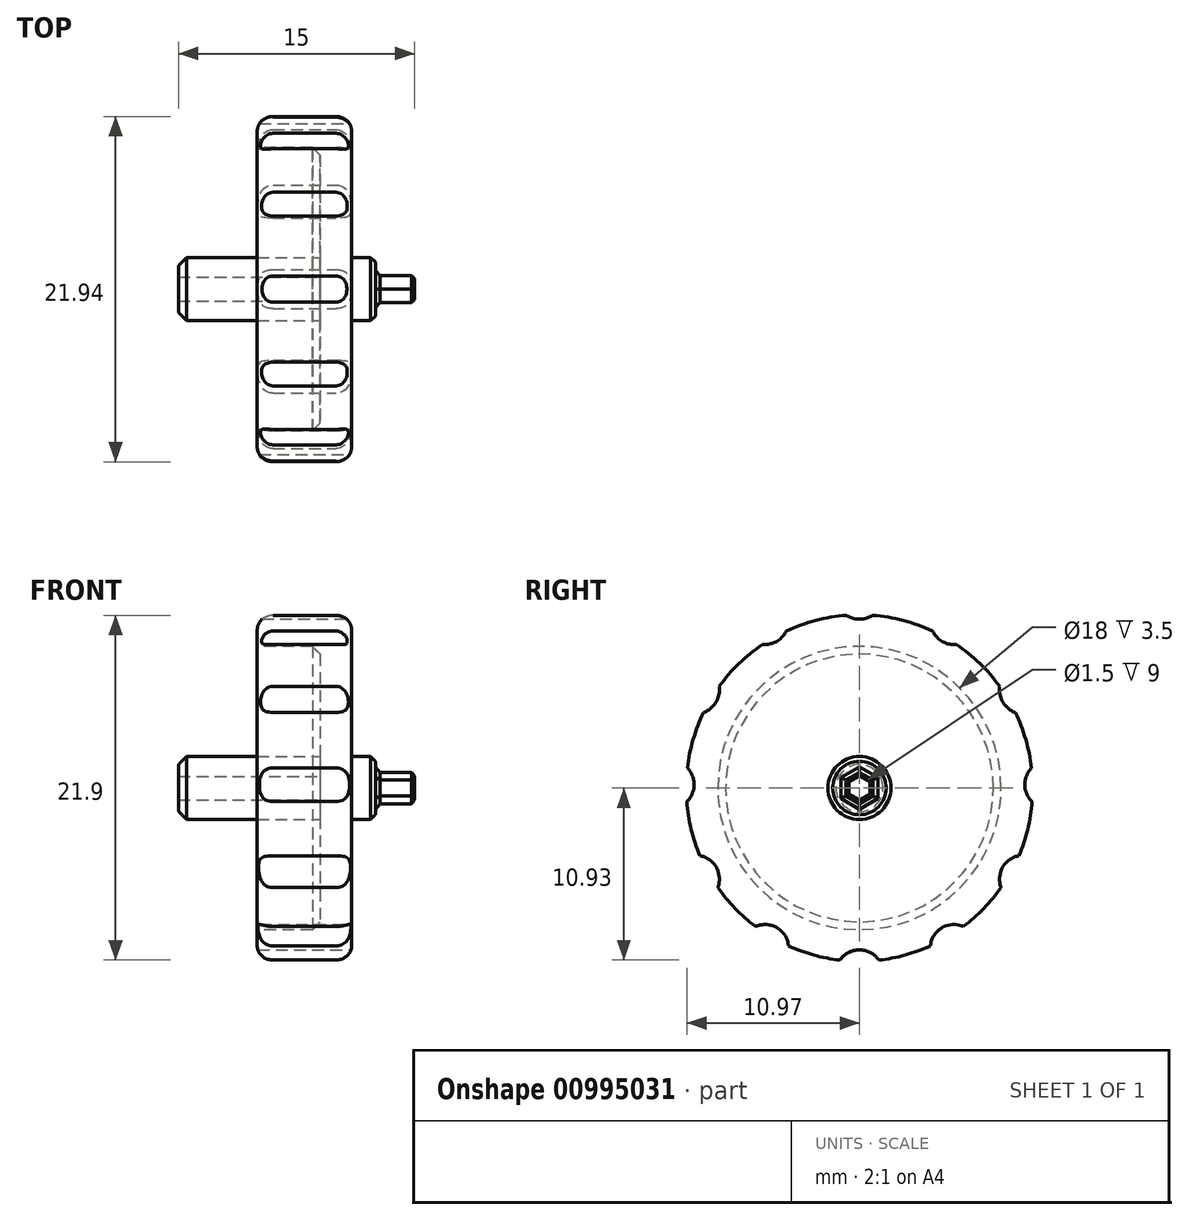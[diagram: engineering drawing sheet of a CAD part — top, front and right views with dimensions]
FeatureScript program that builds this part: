
annotation { "Feature Type Name" : "Feature", "Feature Type Description" : "" }
export const myFeature = defineFeature(function(context is Context, id is Id, definition is map)
    precondition{}
    {
        {
            var Q0;
            Q0=qCreatedBy(makeId("Right.planeOp"),FACE);
            var sketch = newSketch(context, id + "F0", { "sketchPlane" : qUnion([Q0])});
            skCircle(sketch, "E0", {"center": v(0, 0) * mm, "radius": 11 * mm});
            skSolve(sketch);
        }
        {
            var Q0;
            Q0=qSketchRegion(id+"F0",true);
            extrude(context, id + "F1", {"entities" : qUnion([Q0]), "endBound" : BoundingType.SYMMETRIC, "depth" : 6 * mm});
        }
        {
            var Q0;
            Q0=makeQuery(id+"F1.opExtrude","CAP_EDGE",EDGE,{"disambiguationData":[OSD([sQuery(id+"F0.wireOp",EDGE,"E0")])],"isStart":true});
            var Q1;
            Q1=makeQuery(id+"F1.opExtrude","CAP_EDGE",EDGE,{"disambiguationData":[OSD([sQuery(id+"F0.wireOp",EDGE,"E0")])],"isStart":false});
            fillet(context, id + "F2", {"entities" : qUnion([Q0, Q1]), "radius" : 1 * mm, "tangentPropagation" : true, "allowEdgeOverflow" : false});
        }
        {
            var Q0;
            Q0=makeQuery(id+"F1.opExtrude","CAP_FACE",FACE,{"disambiguationData":[OSD([sQuery(id+"F0.wireOp",EDGE,"E0")])],"isStart":true});
            var sketch = newSketch(context, id + "F3", { "sketchPlane" : qUnion([Q0])});
            skCircle(sketch, "E1", {"center": v(0, 0) * mm, "radius": 9 * mm});
            skSolve(sketch);
        }
        {
            var Q0;
            Q0=qSketchRegion(id+"F3",true);
            extrude(context, id + "F4", {"entities" : qUnion([Q0]), "operationType" : NewBodyOperationType.REMOVE, "oppositeDirection" : true, "depth" : 4 * mm});
        }
        {
            var Q0;
            Q0=makeQuery(id+"F4.boolean.opBoolean","COPY",FACE,{"derivedFrom":makeQuery(id+"F4.opExtrude","CAP_FACE",FACE,{"disambiguationData":[OSD([sQuery(id+"F3.wireOp",EDGE,"E1")])],"isStart":false})});
            var sketch = newSketch(context, id + "F5", { "sketchPlane" : qUnion([Q0])});
            skCircle(sketch, "E2", {"center": v(0, 0) * mm, "radius": 2 * mm});
            skCircle(sketch, "E3", {"center": v(0, 0) * mm, "radius": 0.75 * mm});
            skSolve(sketch);
        }
        {
            var Q0;
            Q0=qSketchRegion(id+"F5",true);
            extrude(context, id + "F6", {"entities" : qUnion([Q0]), "operationType" : NewBodyOperationType.ADD, "depth" : 9 * mm});
        }
        {
            var Q0;
            Q0=makeQuery(id+"F1.opExtrude","CAP_FACE",FACE,{"disambiguationData":[OSD([sQuery(id+"F0.wireOp",EDGE,"E0")])],"isStart":false});
            var sketch = newSketch(context, id + "F7", { "sketchPlane" : qUnion([Q0])});
            skCircle(sketch, "E4", {"center": v(0, 0) * mm, "radius": 2 * mm});
            skSolve(sketch);
        }
        {
            var Q0;
            Q0=qSketchRegion(id+"F7",true);
            extrude(context, id + "F8", {"entities" : qUnion([Q0]), "operationType" : NewBodyOperationType.ADD, "depth" : 1.5 * mm});
        }
        {
            var Q0;
            Q0=makeQuery(id+"F8.opExtrude","CAP_FACE",FACE,{"disambiguationData":[OSD([sQuery(id+"F7.wireOp",EDGE,"E4")])],"isStart":false});
            var sketch = newSketch(context, id + "F9", { "sketchPlane" : qUnion([Q0])});
            skCircle(sketch, "E5.cCircle", {"center": v(0, 0) * mm, "radius": 1 * mm, "construction": true});
            skLineSegment(sketch, "E5.0", {"start": v(0.86, 0.5) * mm, "end": v(0.87, -0.5) * mm});
            skLineSegment(sketch, "E5.1", {"start": v(0.86, -0.5) * mm, "end": v(0, -1) * mm});
            skLineSegment(sketch, "E5.2", {"start": v(0, -1) * mm, "end": v(-0.86, -0.5) * mm});
            skLineSegment(sketch, "E5.3", {"start": v(-0.86, -0.5) * mm, "end": v(-0.87, 0.5) * mm});
            skLineSegment(sketch, "E5.4", {"start": v(-0.87, 0.5) * mm, "end": v(0, 1) * mm});
            skLineSegment(sketch, "E5.5", {"start": v(0, 1) * mm, "end": v(0.86, 0.5) * mm});
            skLineSegment(sketch, "E6", {"start": v(0, 0.15) * mm, "end": v(0, 0.7) * mm, "construction": true});
            skSolve(sketch);
        }
        {
            var Q0;
            Q0=qSketchRegion(id+"F9",true);
            extrude(context, id + "F10", {"entities" : qUnion([Q0]), "operationType" : NewBodyOperationType.ADD, "offsetDistance" : 25 * mm, "depth" : 2.5 * mm});
        }
        {
            var Q0;
            Q0=makeQuery(id+"F6.opExtrude","CAP_EDGE",EDGE,{"disambiguationData":[OSD([sQuery(id+"F5.wireOp",EDGE,"E2")])],"isStart":false});
            chamfer(context, id + "F11", {"entities" : qUnion([Q0]), "width" : 0.5 * mm, "tangentPropagation" : true});
        }
        {
            var Q0;
            Q0=makeQuery(id+"F8.opExtrude","CAP_EDGE",EDGE,{"disambiguationData":[OSD([sQuery(id+"F7.wireOp",EDGE,"E4")])],"isStart":true});
            var Q1;
            Q1=makeQuery(id+"F6.opExtrude","CAP_EDGE",EDGE,{"disambiguationData":[OSD([sQuery(id+"F5.wireOp",EDGE,"E2")])],"isStart":true});
            var Q2;
            Q2=makeQuery(id+"F4.boolean.opBoolean","COPY",EDGE,{"derivedFrom":makeQuery(id+"F4.opExtrude","CAP_EDGE",EDGE,{"disambiguationData":[OSD([sQuery(id+"F3.wireOp",EDGE,"E1")])],"isStart":false})});
            chamfer(context, id + "F12", {"entities" : qUnion([Q0, Q1, Q2]), "width" : 0.5 * mm, "tangentPropagation" : true});
        }
        {
            var Q0;
            Q0=qCreatedBy(makeId("Right.planeOp"),FACE);
            var sketch = newSketch(context, id + "F13", { "sketchPlane" : qUnion([Q0])});
            skLineSegment(sketch, "E7", {"start": v(0, 4.49) * mm, "end": v(0, 7.48) * mm, "construction": true});
            skCircle(sketch, "E8", {"center": v(0, 12.22) * mm, "radius": 1.5 * mm});
            skCircle(sketch, "E9.1.0", {"center": v(-6, 10.61) * mm, "radius": 1.5 * mm});
            skCircle(sketch, "E9.2.0", {"center": v(-10.4, 6.22) * mm, "radius": 1.5 * mm});
            skCircle(sketch, "E9.3.0", {"center": v(-12, 0.22) * mm, "radius": 1.5 * mm});
            skCircle(sketch, "E9.4.0", {"center": v(-10.4, -5.78) * mm, "radius": 1.5 * mm});
            skCircle(sketch, "E9.5.0", {"center": v(-6, -10.17) * mm, "radius": 1.5 * mm});
            skCircle(sketch, "E9.6.0", {"center": v(0, -11.78) * mm, "radius": 1.5 * mm});
            skCircle(sketch, "E9.7.0", {"center": v(6, -10.17) * mm, "radius": 1.5 * mm});
            skCircle(sketch, "E9.8.0", {"center": v(10.4, -5.78) * mm, "radius": 1.5 * mm});
            skCircle(sketch, "E9.9.0", {"center": v(12, 0.22) * mm, "radius": 1.5 * mm});
            skCircle(sketch, "E9.10.0", {"center": v(10.4, 6.22) * mm, "radius": 1.5 * mm});
            skCircle(sketch, "E9.11.0", {"center": v(6, 10.61) * mm, "radius": 1.5 * mm});
            skPoint(sketch, "E9.center", {"position": v(0, 0.22) * mm});
            skSolve(sketch);
        }
        {
            var Q0;
            Q0=qSketchRegion(id+"F13",true);
            extrude(context, id + "F14", {"entities" : qUnion([Q0]), "operationType" : NewBodyOperationType.REMOVE, "endBound" : BoundingType.SYMMETRIC, "oppositeDirection" : true, "depth" : 25 * mm, "offsetDistance" : 25 * mm});
        }
        {
            var Q0;
            Q0=makeQuery(id+"F8.opExtrude","CAP_FACE",FACE,{"disambiguationData":[OSD([sQuery(id+"F7.wireOp",EDGE,"E4")])],"isStart":false});
            chamfer(context, id + "F15", {"entities" : qUnion([Q0]), "width" : 0.3 * mm, "tangentPropagation" : true});
        }
        {
            var Q0;
            Q0=makeQuery(id+"F10.opExtrude","CAP_FACE",FACE,{"disambiguationData":[OSD([sQuery(id+"F9.wireOp",EDGE,"E5.0"),sQuery(id+"F9.wireOp",EDGE,"E5.1"),sQuery(id+"F9.wireOp",EDGE,"E5.2"),sQuery(id+"F9.wireOp",EDGE,"E5.3"),sQuery(id+"F9.wireOp",EDGE,"E5.4"),sQuery(id+"F9.wireOp",EDGE,"E5.5")])],"isStart":false});
            chamfer(context, id + "F16", {"entities" : qUnion([Q0]), "width" : 0.2 * mm, "tangentPropagation" : true});
        }
    });
